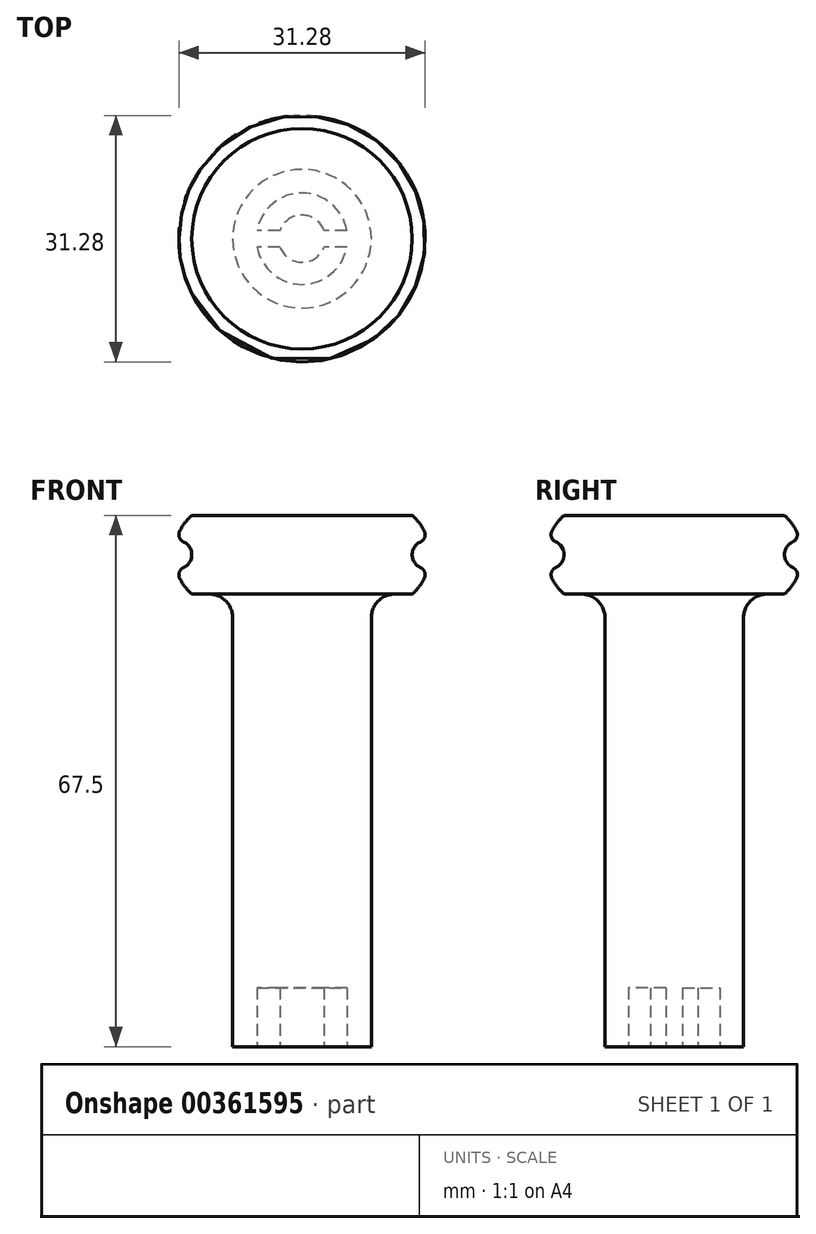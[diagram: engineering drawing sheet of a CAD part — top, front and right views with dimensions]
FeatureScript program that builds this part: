
annotation { "Feature Type Name" : "Feature", "Feature Type Description" : "" }
export const myFeature = defineFeature(function(context is Context, id is Id, definition is map)
    precondition{}
    {
        {
            var Q0;
            Q0=qCreatedBy(makeId("Top.planeOp"),FACE);
            var sketch = newSketch(context, id + "F0", { "sketchPlane" : qUnion([Q0])});
            skArc(sketch, "E0", {"start": v(-5.7, -1.05) * mm, "mid": v(0, -5.8) * mm, "end": v(5.7, -1.05) * mm});
            skArc(sketch, "E1", {"start": v(-2.81, -1.05) * mm, "mid": v(0, -3) * mm, "end": v(2.81, -1.05) * mm});
            skCircle(sketch, "E2", {"center": v(0, 0) * mm, "radius": 8.8 * mm});
            skLineSegment(sketch, "E3.bottom", {"start": v(5.7, -1.05) * mm, "end": v(2.81, -1.05) * mm});
            skLineSegment(sketch, "E3.top", {"start": v(5.7, 1.05) * mm, "end": v(2.81, 1.05) * mm});
            skPoint(sketch, "E3.right.end.orphan", {"position": v(-7.05, 1.05) * mm});
            skPoint(sketch, "E4.orphan", {"position": v(-7.05, -1.05) * mm});
            skLineSegment(sketch, "E5.trimOffspring", {"start": v(-2.81, 1.05) * mm, "end": v(-5.7, 1.05) * mm});
            skLineSegment(sketch, "E6.trimOffspring", {"start": v(-2.81, -1.05) * mm, "end": v(-5.7, -1.05) * mm});
            skArc(sketch, "E7.trimOffspring", {"start": v(2.81, 1.05) * mm, "mid": v(0, 3) * mm, "end": v(-2.81, 1.05) * mm});
            skArc(sketch, "E8.trimOffspring", {"start": v(5.7, 1.05) * mm, "mid": v(0, 5.8) * mm, "end": v(-5.7, 1.05) * mm});
            skPoint(sketch, "E9.orphan", {"position": v(7.05, 1.05) * mm});
            skPoint(sketch, "E10.orphan", {"position": v(7.05, -1.05) * mm});
            skSolve(sketch);
        }
        {
            var Q0;
            Q0=makeQuery(id+"F0.imprint","IMPRINT",FACE,{"disambiguationData":[TD([[makeQuery(id+"F0.imprint","IMPRINT",EDGE,{"derivedFrom":sQuery(id+"F0.wireOp",EDGE,"E0")}),-1.0]])]});
            extrude(context, id + "F1", {"entities" : qUnion([Q0]), "depth" : 7.5 * mm});
        }
        {
            var Q0;
            Q0=makeQuery(id+"F1.opExtrude","CAP_FACE",FACE,{"disambiguationData":[OSD([sQuery(id+"F0.wireOp",EDGE,"E0"),sQuery(id+"F0.wireOp",EDGE,"E1"),sQuery(id+"F0.wireOp",EDGE,"E2"),sQuery(id+"F0.wireOp",EDGE,"E3.bottom"),sQuery(id+"F0.wireOp",EDGE,"E3.top"),sQuery(id+"F0.wireOp",EDGE,"E5.trimOffspring"),sQuery(id+"F0.wireOp",EDGE,"E6.trimOffspring"),sQuery(id+"F0.wireOp",EDGE,"E7.trimOffspring"),sQuery(id+"F0.wireOp",EDGE,"E8.trimOffspring")])],"isStart":false});
            var sketch = newSketch(context, id + "F2", { "sketchPlane" : qUnion([Q0])});
            skCircle(sketch, "E11.0", {"center": v(0, 0) * mm, "radius": 8.8 * mm});
            skSolve(sketch);
        }
        {
            var Q0;
            Q0=makeQuery(id+"F2.imprint","IMPRINT",FACE,{"disambiguationData":[TD([[makeQuery(id+"F2.imprint","IMPRINT",EDGE,{"derivedFrom":makeQuery(id+"F1.opExtrude","CAP_EDGE",EDGE,{"disambiguationData":[OSD([sQuery(id+"F0.wireOp",EDGE,"E3.top")])],"isStart":false})}),-1.0]])]});
            var Q1;
            Q1=makeQuery(id+"F2.imprint","IMPRINT",FACE,{"disambiguationData":[TD([[makeQuery(id+"F2.imprint","IMPRINT",EDGE,{"derivedFrom":makeQuery(id+"F1.opExtrude","CAP_EDGE",EDGE,{"disambiguationData":[OSD([sQuery(id+"F0.wireOp",EDGE,"E0")])],"isStart":false})}),1.0]])]});
            var Q2;
            Q2=makeQuery(id+"F2.imprint","IMPRINT",FACE,{"disambiguationData":[TD([[makeQuery(id+"F2.imprint","IMPRINT",EDGE,{"derivedFrom":sQuery(id+"F2.wireOp",EDGE,"E11.0")}),1.0]])]});
            extrude(context, id + "F3", {"entities" : qUnion([Q0, Q1, Q2]), "operationType" : NewBodyOperationType.ADD, "depth" : 55 * mm});
        }
        {
            var Q0;
            Q0=makeQuery(id+"F3.opExtrude","CAP_FACE",FACE,{"disambiguationData":[OSD([sQuery(id+"F2.wireOp",EDGE,"E11.0")])],"isStart":false});
            var sketch = newSketch(context, id + "F4", { "sketchPlane" : qUnion([Q0])});
            skCircle(sketch, "E12", {"center": v(0, 0) * mm, "radius": 14 * mm});
            skSolve(sketch);
        }
        {
            var Q0;
            Q0=makeQuery(id+"F4.imprint","IMPRINT",FACE,{"disambiguationData":[TD([[makeQuery(id+"F4.imprint","IMPRINT",EDGE,{"derivedFrom":sQuery(id+"F4.wireOp",EDGE,"E12")}),1.0]])]});
            var Q1;
            Q1=makeQuery(id+"F4.imprint","IMPRINT",FACE,{"disambiguationData":[TD([[makeQuery(id+"F4.imprint","IMPRINT",EDGE,{"derivedFrom":makeQuery(id+"F3.opExtrude","CAP_EDGE",EDGE,{"disambiguationData":[OSD([sQuery(id+"F2.wireOp",EDGE,"E11.0")])],"isStart":false})}),1.0]])]});
            extrude(context, id + "F5", {"entities" : qUnion([Q0, Q1]), "operationType" : NewBodyOperationType.ADD, "endBound" : BoundingType.SYMMETRIC, "oppositeDirection" : true, "depth" : 10 * mm});
        }
        {
            var Q0;
            Q0=qCreatedBy(makeId("Front.planeOp"),FACE);
            var sketch = newSketch(context, id + "F6", { "sketchPlane" : qUnion([Q0])});
            skLineSegment(sketch, "E13", {"start": v(-14, 57.5) * mm, "end": v(-14, 67.5) * mm});
            skArc(sketch, "E14", {"start": v(-16, 60.71) * mm, "mid": v(-14, 62.5) * mm, "end": v(-16, 64.29) * mm});
            skPoint(sketch, "E14.centerSnap0", {"position": v(-14, 62.5) * mm});
            skArc(sketch, "E15", {"start": v(-14, 67.5) * mm, "mid": v(-15.23, 66.04) * mm, "end": v(-16, 64.29) * mm});
            skArc(sketch, "E16.trimOffspring", {"start": v(-16, 60.71) * mm, "mid": v(-15.23, 58.96) * mm, "end": v(-14, 57.5) * mm});
            skLineSegment(sketch, "E17", {"start": v(0, 0) * mm, "end": v(0, 71.31) * mm, "construction": true});
            skSolve(sketch);
        }
        {
            var Q0;
            {var subQ0=sQuery(id+"F6.wireOp",EDGE,"E15");Q0=makeQuery(id+"F6.imprint","IMPRINT",FACE,{"disambiguationData":[TD([[makeQuery(id+"F6.imprint","IMPRINT",EDGE,{"derivedFrom":subQ0}),1.0]])]});}
            var Q1;
            {var subQ0=sQuery(id+"F6.wireOp",EDGE,"E16.trimOffspring");Q1=makeQuery(id+"F6.imprint","IMPRINT",FACE,{"disambiguationData":[TD([[makeQuery(id+"F6.imprint","IMPRINT",EDGE,{"derivedFrom":subQ0}),1.0]])]});}
            var Q2;
            Q2=sQuery(id+"F6.wireOp",EDGE,"E17");
            var Q3;
            Q3=sQuery(id+"F6.wireOp",EDGE,"E15");
            var Q4;
            Q4=sQuery(id+"F6.wireOp",EDGE,"E14");
            var Q5;
            Q5=sQuery(id+"F6.wireOp",EDGE,"E16.trimOffspring");
            var Q6;
            Q6=sQuery(id+"F6.wireOp",EDGE,"E17");
            revolve(context, id + "F7", {"operationType" : NewBodyOperationType.ADD, "entities" : qUnion([Q0, Q1]), "surfaceEntities" : qUnion([Q2, Q3, Q4, Q5]), "axis" : qUnion([Q6]), "revolveType" : RevolveType.FULL});
        }
        {
            var Q0;
            Q0=makeQuery(id+"F7.opRevolve","SWEPT_EDGE",EDGE,{"disambiguationData":[OSD([sQuery(id+"F6.wireOp",EDGE,"E14"),sQuery(id+"F6.wireOp",EDGE,"E15")])]});
            var Q1;
            Q1=makeQuery(id+"F7.opRevolve","SWEPT_EDGE",EDGE,{"disambiguationData":[OSD([sQuery(id+"F6.wireOp",EDGE,"E14"),sQuery(id+"F6.wireOp",EDGE,"E16.trimOffspring")])]});
            fillet(context, id + "F8", {"entities" : qUnion([Q0, Q1]), "radius" : 1 * mm, "tangentPropagation" : true, "allowEdgeOverflow" : false});
        }
        {
            var Q0;
            Q0=makeQuery(id+"F5.boolean.opBoolean","INTERSECT",EDGE,{"derivedFrom":[makeQuery(id+"F3.boolean.opBoolean","MERGE",FACE,{"derivedFrom":[makeQuery(id+"F1.opExtrude","SWEPT_FACE",FACE,{"disambiguationData":[OSD([sQuery(id+"F0.wireOp",EDGE,"E2")])]}),makeQuery(id+"F3.opExtrude","SWEPT_FACE",FACE,{"disambiguationData":[OSD([sQuery(id+"F2.wireOp",EDGE,"E11.0")])]})]}),makeQuery(id+"F5.opExtrude","CAP_FACE",FACE,{"disambiguationData":[OSD([sQuery(id+"F4.wireOp",EDGE,"E12")])],"isStart":false})]});
            fillet(context, id + "F9", {"entities" : qUnion([Q0]), "radius" : 3 * mm, "tangentPropagation" : true, "allowEdgeOverflow" : false});
        }
    });
